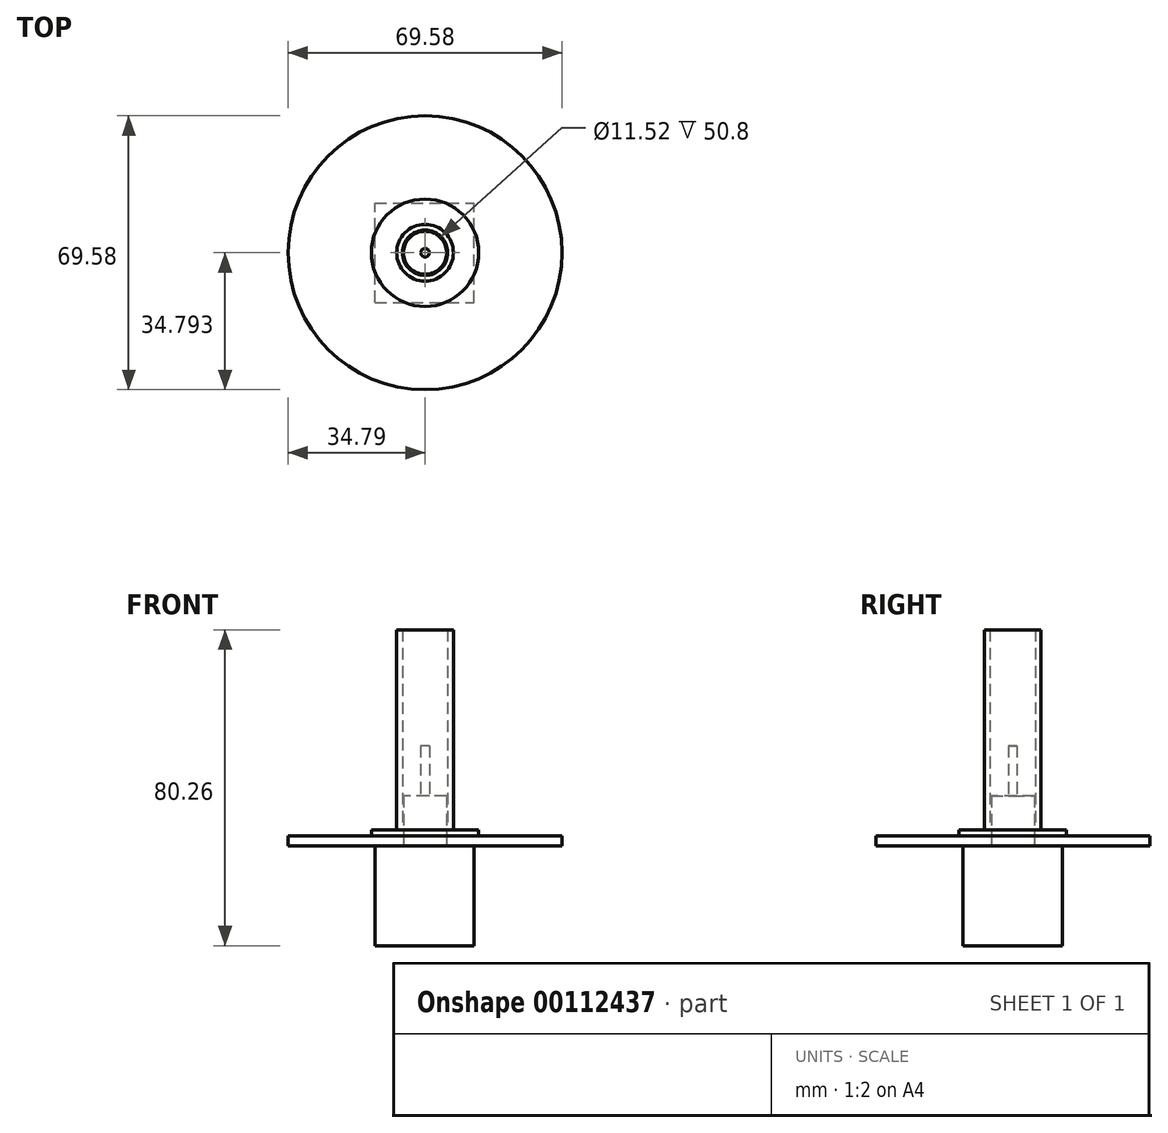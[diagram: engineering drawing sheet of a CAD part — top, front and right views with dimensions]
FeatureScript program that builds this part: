
annotation { "Feature Type Name" : "Feature", "Feature Type Description" : "" }
export const myFeature = defineFeature(function(context is Context, id is Id, definition is map)
    precondition{}
    {
        {
            var Q0;
            Q0=qCreatedBy(makeId("Top.planeOp"),FACE);
            var sketch = newSketch(context, id + "F0", { "sketchPlane" : qUnion([Q0])});
            skLineSegment(sketch, "E0.bottom", {"start": v(0, 0) * mm, "end": v(25.15, 0) * mm});
            skLineSegment(sketch, "E0.top", {"start": v(0, 25.25) * mm, "end": v(25.15, 25.25) * mm});
            skLineSegment(sketch, "E0.left", {"start": v(0, 0) * mm, "end": v(0, 25.25) * mm});
            skLineSegment(sketch, "E0.right", {"start": v(25.15, 0) * mm, "end": v(25.15, 25.25) * mm});
            skSolve(sketch);
        }
        {
            var Q0;
            Q0 = qSketchRegion(id + "F0", true);
            extrude(context, id + "F1", {"entities" : qUnion([Q0]), "depth" : 25.4 * mm});
        }
        {
            var Q0;
            Q0=makeQuery(id+"F1.opExtrude","CAP_FACE",FACE,{"disambiguationData":[OSD([sQuery(id+"F0.wireOp",EDGE,"E0.bottom"),sQuery(id+"F0.wireOp",EDGE,"E0.top"),sQuery(id+"F0.wireOp",EDGE,"E0.left"),sQuery(id+"F0.wireOp",EDGE,"E0.right")])],"isStart":false});
            var sketch = newSketch(context, id + "F2", { "sketchPlane" : qUnion([Q0])});
            skCircle(sketch, "E1", {"center": v(12.72, 12.62) * mm, "radius": 5.47 * mm});
            skSolve(sketch);
        }
        {
            var Q0;
            Q0 = qSketchRegion(id + "F2", true);
            extrude(context, id + "F3", {"entities" : qUnion([Q0]), "operationType" : NewBodyOperationType.ADD, "depth" : 12.7 * mm});
        }
        {
            var Q0;
            Q0=makeQuery(id+"F3.opExtrude","CAP_FACE",FACE,{"disambiguationData":[OSD([sQuery(id+"F2.wireOp",EDGE,"E1")])],"isStart":false});
            var sketch = newSketch(context, id + "F4", { "sketchPlane" : qUnion([Q0])});
            skCircle(sketch, "E2", {"center": v(12.72, 12.62) * mm, "radius": 1.08 * mm});
            skSolve(sketch);
        }
        {
            var Q0;
            Q0 = qSketchRegion(id + "F4", true);
            extrude(context, id + "F5", {"entities" : qUnion([Q0]), "depth" : 12.7 * mm});
        }
        {
            var Q0;
            Q0=makeQuery(id+"F1.opExtrude","CAP_FACE",FACE,{"disambiguationData":[OSD([sQuery(id+"F0.wireOp",EDGE,"E0.bottom"),sQuery(id+"F0.wireOp",EDGE,"E0.top"),sQuery(id+"F0.wireOp",EDGE,"E0.left"),sQuery(id+"F0.wireOp",EDGE,"E0.right")])],"isStart":false});
            var sketch = newSketch(context, id + "F6", { "sketchPlane" : qUnion([Q0])});
            skCircle(sketch, "E3", {"center": v(12.72, 12.62) * mm, "radius": 34.79 * mm});
            skSolve(sketch);
        }
        {
            var Q0;
            Q0 = qSketchRegion(id + "F6", true);
            extrude(context, id + "F7", {"entities" : qUnion([Q0]), "depth" : 2.54 * mm});
        }
        {
            var Q0;
            Q0=makeQuery(id+"F7.opExtrude","CAP_FACE",FACE,{"disambiguationData":[OSD([sQuery(id+"F6.wireOp",EDGE,"E3")])],"isStart":false});
            var sketch = newSketch(context, id + "F8", { "sketchPlane" : qUnion([Q0])});
            skCircle(sketch, "E4", {"center": v(12.72, 12.62) * mm, "radius": 13.64 * mm});
            skSolve(sketch);
        }
        {
            var Q0;
            Q0 = qSketchRegion(id + "F8", true);
            extrude(context, id + "F9", {"entities" : qUnion([Q0]), "depth" : 1.52 * mm});
        }
        {
            var Q0;
            Q0=makeQuery(id+"F9.opExtrude","CAP_FACE",FACE,{"disambiguationData":[OSD([sQuery(id+"F8.wireOp",EDGE,"E4")])],"isStart":false});
            var sketch = newSketch(context, id + "F10", { "sketchPlane" : qUnion([Q0])});
            skCircle(sketch, "E5", {"center": v(12.72, 12.62) * mm, "radius": 7.2 * mm});
            skCircle(sketch, "E6", {"center": v(12.72, 12.62) * mm, "radius": 5.76 * mm});
            skSolve(sketch);
        }
        {
            var Q0;
            Q0 = qSketchRegion(id + "F10", true);
            extrude(context, id + "F11", {"entities" : qUnion([Q0]), "depth" : 50.8 * mm});
        }
    });
